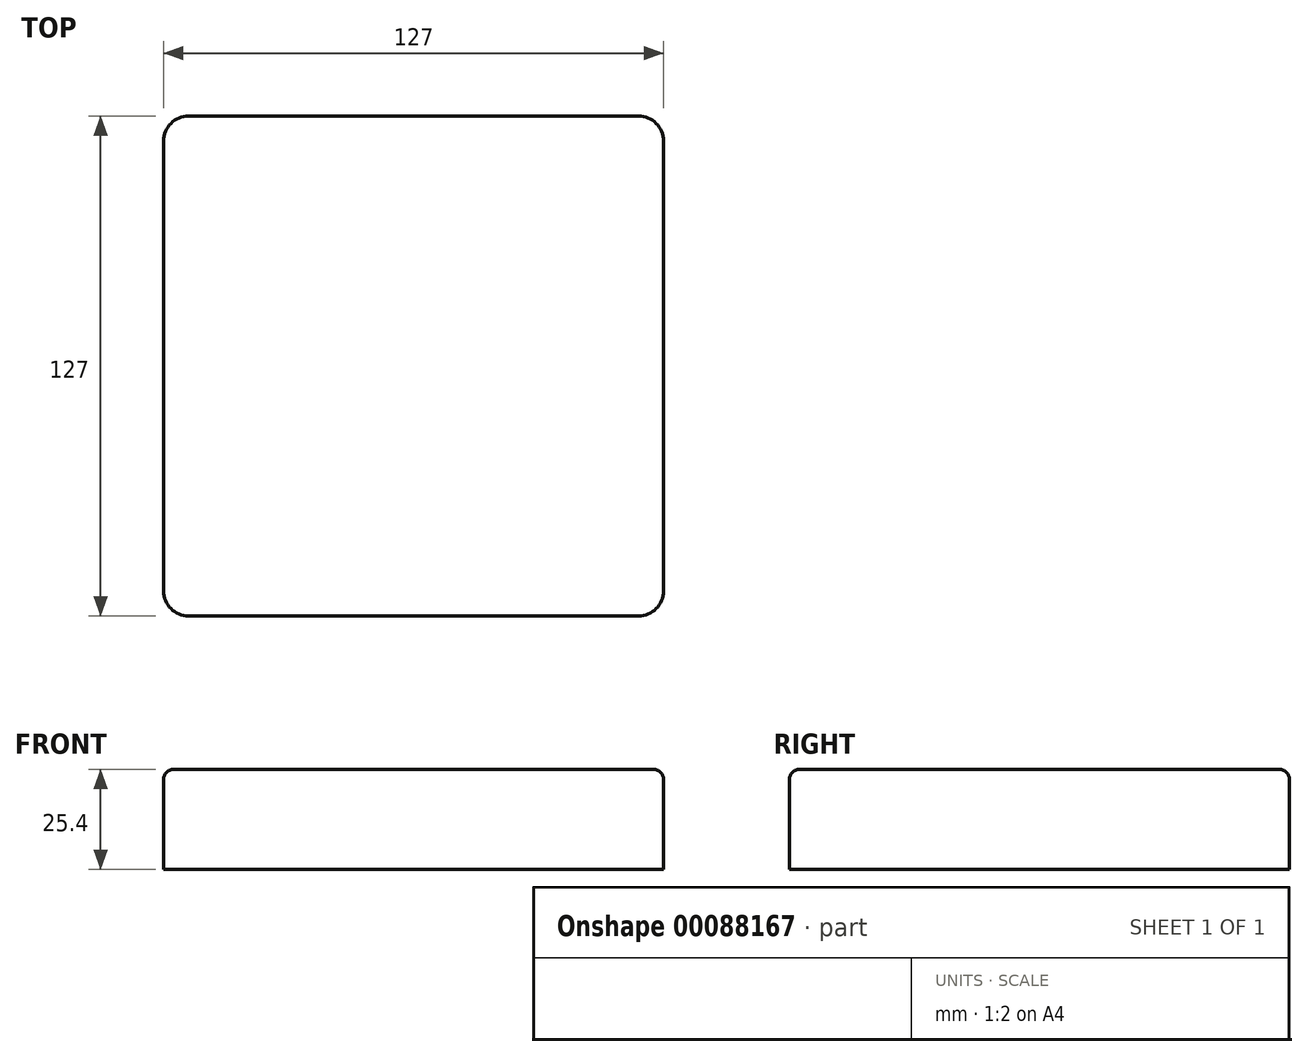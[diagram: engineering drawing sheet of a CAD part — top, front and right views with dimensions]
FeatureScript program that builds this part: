
annotation { "Feature Type Name" : "Feature", "Feature Type Description" : "" }
export const myFeature = defineFeature(function(context is Context, id is Id, definition is map)
    precondition{}
    {
        {
            var Q0;
            Q0=qCreatedBy(makeId("Top.planeOp"),FACE);
            var sketch = newSketch(context, id + "F0", { "sketchPlane" : qUnion([Q0])});
            skLineSegment(sketch, "E0.bottom", {"start": v(-57.15, 63.5) * mm, "end": v(57.15, 63.5) * mm});
            skLineSegment(sketch, "E0.top", {"start": v(-57.15, -63.5) * mm, "end": v(57.15, -63.5) * mm});
            skLineSegment(sketch, "E0.left", {"start": v(-63.5, 57.15) * mm, "end": v(-63.5, -57.15) * mm});
            skLineSegment(sketch, "E0.right", {"start": v(63.5, 57.15) * mm, "end": v(63.5, -57.15) * mm});
            skPoint(sketch, "E1.visualSharp", {"position": v(-63.5, 63.5) * mm});
            skArc(sketch, "E1.filletArc", {"start": v(-57.15, 63.5) * mm, "mid": v(-61.64, 61.64) * mm, "end": v(-63.5, 57.15) * mm});
            skPoint(sketch, "E2.visualSharp", {"position": v(63.5, 63.5) * mm});
            skArc(sketch, "E2.filletArc", {"start": v(63.5, 57.15) * mm, "mid": v(61.64, 61.64) * mm, "end": v(57.15, 63.5) * mm});
            skPoint(sketch, "E3.visualSharp", {"position": v(63.5, -63.5) * mm});
            skArc(sketch, "E3.filletArc", {"start": v(57.15, -63.5) * mm, "mid": v(61.64, -61.64) * mm, "end": v(63.5, -57.15) * mm});
            skPoint(sketch, "E4.visualSharp", {"position": v(-63.5, -63.5) * mm});
            skArc(sketch, "E4.filletArc", {"start": v(-63.5, -57.15) * mm, "mid": v(-61.64, -61.64) * mm, "end": v(-57.15, -63.5) * mm});
            skSolve(sketch);
        }
        {
            var Q0;
            Q0 = qSketchRegion(id + "F0", true);
            extrude(context, id + "F1", {"entities" : qUnion([Q0]), "depth" : 25.4 * mm});
        }
        {
            var Q0;
            Q0=makeQuery(id+"F1.opExtrude","CAP_EDGE",EDGE,{"disambiguationData":[OSD([sQuery(id+"F0.wireOp",EDGE,"E0.right")])],"isStart":false});
            fillet(context, id + "F2", {"entities" : qUnion([Q0]), "radius" : 2.54 * mm, "tangentPropagation" : true, "allowEdgeOverflow" : false});
        }
    });
